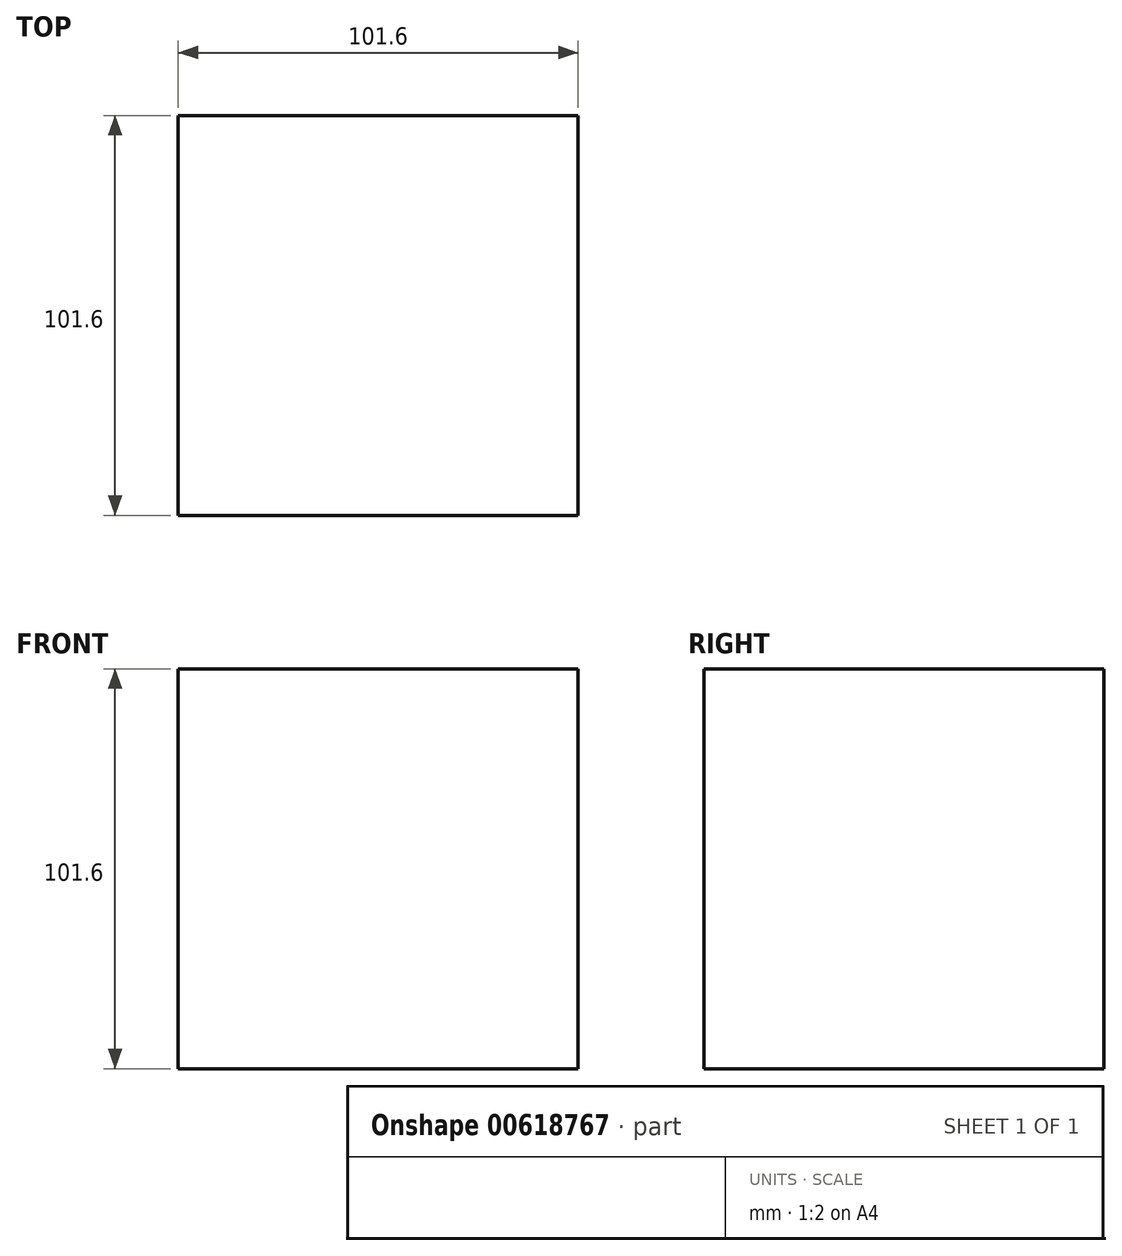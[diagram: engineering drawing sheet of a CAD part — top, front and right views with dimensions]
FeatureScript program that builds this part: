
annotation { "Feature Type Name" : "Feature", "Feature Type Description" : "" }
export const myFeature = defineFeature(function(context is Context, id is Id, definition is map)
    precondition{}
    {
        {
            var Q0;
            Q0=qCreatedBy(makeId("Top.planeOp"),FACE);
            var sketch = newSketch(context, id + "F0", { "sketchPlane" : qUnion([Q0])});
            skLineSegment(sketch, "E0.bottom", {"start": v(50.8, -50.8) * mm, "end": v(-50.8, -50.8) * mm});
            skLineSegment(sketch, "E0.top", {"start": v(50.8, 50.8) * mm, "end": v(-50.8, 50.8) * mm});
            skLineSegment(sketch, "E0.left", {"start": v(50.8, -50.8) * mm, "end": v(50.8, 50.8) * mm});
            skLineSegment(sketch, "E0.right", {"start": v(-50.8, -50.8) * mm, "end": v(-50.8, 50.8) * mm});
            skPoint(sketch, "E0.middle", {"position": v(0, 0) * mm});
            skSolve(sketch);
        }
        {
            var Q0;
            Q0 = qSketchRegion(id + "F0", true);
            extrude(context, id + "F1", {"entities" : qUnion([Q0]), "depth" : 101.6 * mm, "offsetDistance" : 25.4 * mm});
        }
    });
